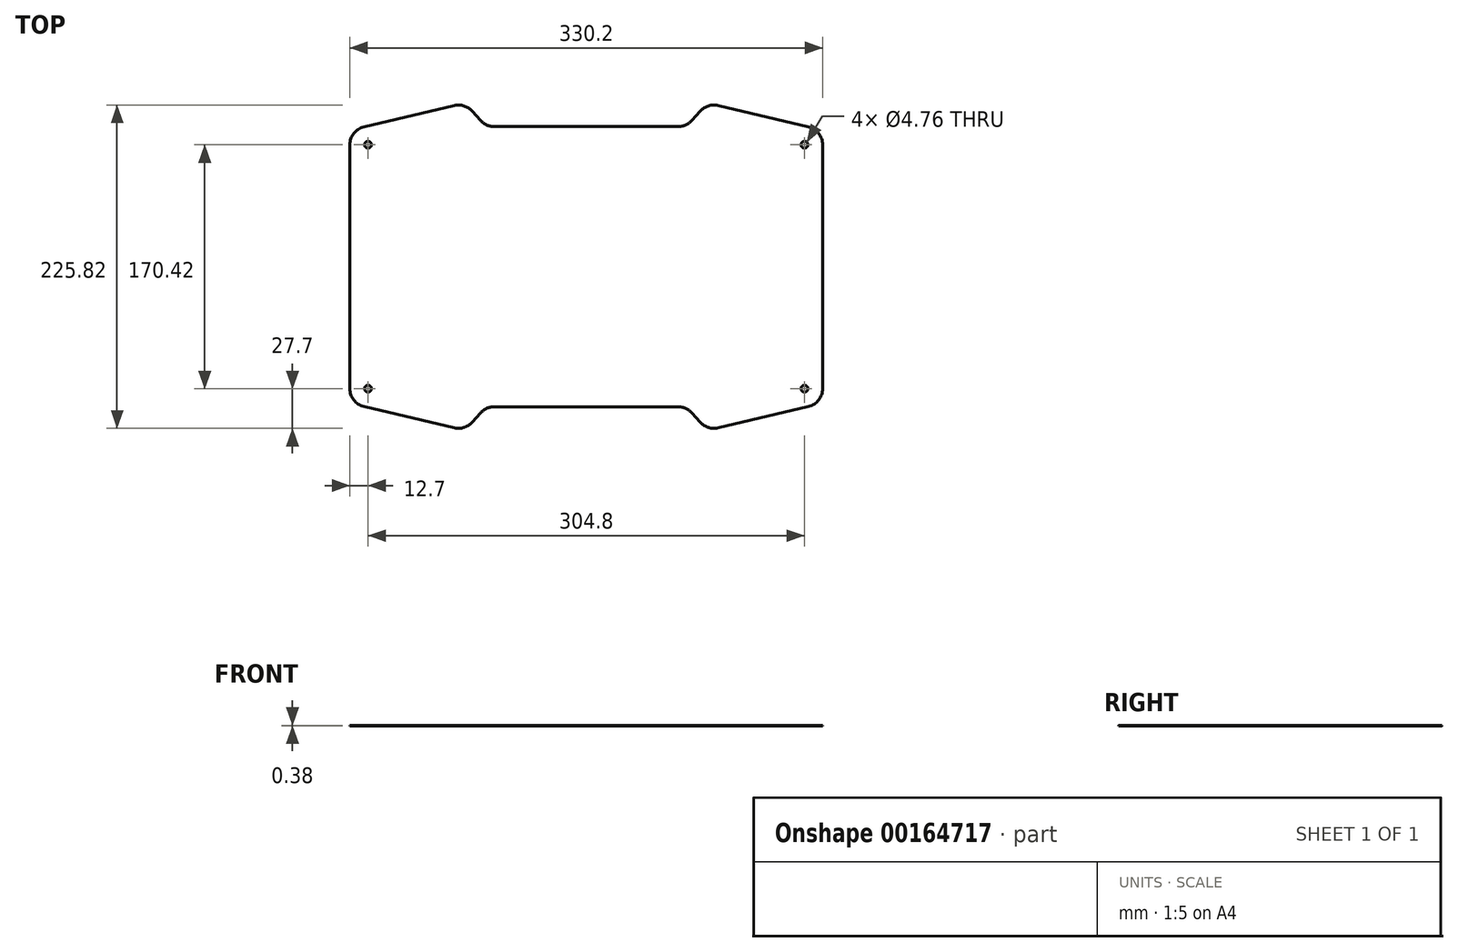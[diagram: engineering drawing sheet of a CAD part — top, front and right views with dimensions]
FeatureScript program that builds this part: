
annotation { "Feature Type Name" : "Feature", "Feature Type Description" : "" }
export const myFeature = defineFeature(function(context is Context, id is Id, definition is map)
    precondition{}
    {
        {
            var Q0;
            Q0=qCreatedBy(makeId("Top.planeOp"),FACE);
            var sketch = newSketch(context, id + "F0", { "sketchPlane" : qUnion([Q0])});
            skLineSegment(sketch, "E0.left", {"start": v(165.1, 95.25) * mm, "end": v(165.1, -95.25) * mm});
            skLineSegment(sketch, "E0.right", {"start": v(-165.1, 95.25) * mm, "end": v(-165.1, -95.25) * mm});
            skPoint(sketch, "E0.middle", {"position": v(0, 0) * mm});
            skLineSegment(sketch, "E1", {"start": v(-165.1, 95.25) * mm, "end": v(-84.78, 114.3) * mm});
            skLineSegment(sketch, "E2", {"start": v(-84.78, 114.3) * mm, "end": v(-69.85, 97.88) * mm});
            skLineSegment(sketch, "E3", {"start": v(-69.85, 97.88) * mm, "end": v(0, 97.88) * mm});
            skLineSegment(sketch, "E4.MirrorCS", {"start": v(165.1, 95.25) * mm, "end": v(84.78, 114.3) * mm});
            skLineSegment(sketch, "E5.MirrorCS", {"start": v(84.78, 114.3) * mm, "end": v(69.85, 97.88) * mm});
            skLineSegment(sketch, "E6.MirrorCS", {"start": v(69.85, 97.88) * mm, "end": v(0, 97.88) * mm});
            skLineSegment(sketch, "E7.MirrorCS", {"start": v(-165.1, -95.25) * mm, "end": v(-84.78, -114.3) * mm});
            skLineSegment(sketch, "E8.MirrorCS", {"start": v(-84.78, -114.3) * mm, "end": v(-69.85, -97.88) * mm});
            skLineSegment(sketch, "E9.MirrorCS", {"start": v(-69.85, -97.88) * mm, "end": v(0, -97.88) * mm});
            skLineSegment(sketch, "E10.MirrorCS", {"start": v(69.85, -97.88) * mm, "end": v(0, -97.88) * mm});
            skLineSegment(sketch, "E11.MirrorCS", {"start": v(84.78, -114.3) * mm, "end": v(69.85, -97.88) * mm});
            skLineSegment(sketch, "E12.MirrorCS", {"start": v(165.1, -95.25) * mm, "end": v(84.78, -114.3) * mm});
            skPoint(sketch, "E13.orphan", {"position": v(-165.1, 114.3) * mm});
            skPoint(sketch, "E14.orphan", {"position": v(165.1, 114.3) * mm});
            skPoint(sketch, "E15.orphan", {"position": v(165.1, -114.3) * mm});
            skPoint(sketch, "E16.orphan", {"position": v(-165.1, -114.3) * mm});
            skSolve(sketch);
        }
        {
            var Q0;
            Q0 = qSketchRegion(id + "F0", true);
            extrude(context, id + "F1", {"entities" : qUnion([Q0]), "depth" : 0.38 * mm});
        }
        {
            var Q0;
            Q0=makeQuery(id+"F1.opExtrude","SWEPT_EDGE",EDGE,{"disambiguationData":[OSD([sQuery(id+"F0.wireOp",EDGE,"E0.right"),sQuery(id+"F0.wireOp",EDGE,"E7.MirrorCS")])]});
            var Q1;
            Q1=makeQuery(id+"F1.opExtrude","SWEPT_EDGE",EDGE,{"disambiguationData":[OSD([sQuery(id+"F0.wireOp",EDGE,"E7.MirrorCS"),sQuery(id+"F0.wireOp",EDGE,"E8.MirrorCS")])]});
            var Q2;
            Q2=makeQuery(id+"F1.opExtrude","SWEPT_EDGE",EDGE,{"disambiguationData":[OSD([sQuery(id+"F0.wireOp",EDGE,"E8.MirrorCS"),sQuery(id+"F0.wireOp",EDGE,"E9.MirrorCS")])]});
            var Q3;
            Q3=makeQuery(id+"F1.opExtrude","SWEPT_EDGE",EDGE,{"disambiguationData":[OSD([sQuery(id+"F0.wireOp",EDGE,"E10.MirrorCS"),sQuery(id+"F0.wireOp",EDGE,"E11.MirrorCS")])]});
            var Q4;
            Q4=makeQuery(id+"F1.opExtrude","SWEPT_EDGE",EDGE,{"disambiguationData":[OSD([sQuery(id+"F0.wireOp",EDGE,"E11.MirrorCS"),sQuery(id+"F0.wireOp",EDGE,"E12.MirrorCS")])]});
            var Q5;
            Q5=makeQuery(id+"F1.opExtrude","SWEPT_EDGE",EDGE,{"disambiguationData":[OSD([sQuery(id+"F0.wireOp",EDGE,"E0.left"),sQuery(id+"F0.wireOp",EDGE,"E12.MirrorCS")])]});
            var Q6;
            Q6=makeQuery(id+"F1.opExtrude","SWEPT_EDGE",EDGE,{"disambiguationData":[OSD([sQuery(id+"F0.wireOp",EDGE,"E0.left"),sQuery(id+"F0.wireOp",EDGE,"E4.MirrorCS")])]});
            var Q7;
            Q7=makeQuery(id+"F1.opExtrude","SWEPT_EDGE",EDGE,{"disambiguationData":[OSD([sQuery(id+"F0.wireOp",EDGE,"E4.MirrorCS"),sQuery(id+"F0.wireOp",EDGE,"E5.MirrorCS")])]});
            var Q8;
            Q8=makeQuery(id+"F1.opExtrude","SWEPT_EDGE",EDGE,{"disambiguationData":[OSD([sQuery(id+"F0.wireOp",EDGE,"E5.MirrorCS"),sQuery(id+"F0.wireOp",EDGE,"E6.MirrorCS")])]});
            var Q9;
            Q9=makeQuery(id+"F1.opExtrude","SWEPT_EDGE",EDGE,{"disambiguationData":[OSD([sQuery(id+"F0.wireOp",EDGE,"E2"),sQuery(id+"F0.wireOp",EDGE,"E3")])]});
            var Q10;
            Q10=makeQuery(id+"F1.opExtrude","SWEPT_EDGE",EDGE,{"disambiguationData":[OSD([sQuery(id+"F0.wireOp",EDGE,"E1"),sQuery(id+"F0.wireOp",EDGE,"E2")])]});
            var Q11;
            Q11=makeQuery(id+"F1.opExtrude","SWEPT_EDGE",EDGE,{"disambiguationData":[OSD([sQuery(id+"F0.wireOp",EDGE,"E0.right"),sQuery(id+"F0.wireOp",EDGE,"E1")])]});
            fillet(context, id + "F2", {"entities" : qUnion([Q0, Q1, Q2, Q3, Q4, Q5, Q6, Q7, Q8, Q9, Q10, Q11]), "radius" : 12.7 * mm, "tangentPropagation" : true, "allowEdgeOverflow" : false});
        }
        {
            var Q0;
            Q0=makeQuery(id+"F1.opExtrude","CAP_FACE",FACE,{"disambiguationData":[OSD([sQuery(id+"F0.wireOp",EDGE,"E0.left"),sQuery(id+"F0.wireOp",EDGE,"E0.right"),sQuery(id+"F0.wireOp",EDGE,"E1"),sQuery(id+"F0.wireOp",EDGE,"E2"),sQuery(id+"F0.wireOp",EDGE,"E3"),sQuery(id+"F0.wireOp",EDGE,"E4.MirrorCS"),sQuery(id+"F0.wireOp",EDGE,"E5.MirrorCS"),sQuery(id+"F0.wireOp",EDGE,"E6.MirrorCS"),sQuery(id+"F0.wireOp",EDGE,"E7.MirrorCS"),sQuery(id+"F0.wireOp",EDGE,"E8.MirrorCS"),sQuery(id+"F0.wireOp",EDGE,"E9.MirrorCS"),sQuery(id+"F0.wireOp",EDGE,"E10.MirrorCS"),sQuery(id+"F0.wireOp",EDGE,"E11.MirrorCS"),sQuery(id+"F0.wireOp",EDGE,"E12.MirrorCS")])],"isStart":false});
            var sketch = newSketch(context, id + "F3", { "sketchPlane" : qUnion([Q0])});
            skPoint(sketch, "E17", {"position": v(152.4, -85.2) * mm});
            skPoint(sketch, "E18.MirrorP", {"position": v(-152.4, -85.2) * mm});
            skPoint(sketch, "E19.MirrorP", {"position": v(152.4, 85.2) * mm});
            skPoint(sketch, "E20.MirrorP", {"position": v(-152.4, 85.2) * mm});
            skSolve(sketch);
        }
        {
            var Q0;
            Q0=sQuery(id+"F3.wireOp",VERTEX,"E17");
            var Q1;
            Q1=sQuery(id+"F3.wireOp",VERTEX,"E18.MirrorP");
            var Q2;
            Q2=sQuery(id+"F3.wireOp",VERTEX,"E20.MirrorP");
            var Q3;
            Q3=sQuery(id+"F3.wireOp",VERTEX,"E19.MirrorP");
            var Q4;
            Q4=makeQuery(id+"F1.opExtrude","SWEPT_BODY",BODY,{"disambiguationData":[OSD([sQuery(id+"F0.wireOp",EDGE,"E0.left"),sQuery(id+"F0.wireOp",EDGE,"E0.right"),sQuery(id+"F0.wireOp",EDGE,"E1"),sQuery(id+"F0.wireOp",EDGE,"E2"),sQuery(id+"F0.wireOp",EDGE,"E3"),sQuery(id+"F0.wireOp",EDGE,"E4.MirrorCS"),sQuery(id+"F0.wireOp",EDGE,"E5.MirrorCS"),sQuery(id+"F0.wireOp",EDGE,"E6.MirrorCS"),sQuery(id+"F0.wireOp",EDGE,"E7.MirrorCS"),sQuery(id+"F0.wireOp",EDGE,"E8.MirrorCS"),sQuery(id+"F0.wireOp",EDGE,"E9.MirrorCS"),sQuery(id+"F0.wireOp",EDGE,"E10.MirrorCS"),sQuery(id+"F0.wireOp",EDGE,"E11.MirrorCS"),sQuery(id+"F0.wireOp",EDGE,"E12.MirrorCS")])]});
            hole(context, id + "F4", {"style" : HoleStyle.SIMPLE, "endStyle" : HoleEndStyle.BLIND, "holeDiameter" : 4.76 * mm, "holeDepth" : 6.73 * mm, "locations" : qUnion([Q0, Q1, Q2, Q3]), "scope" : qUnion([Q4])});
        }
    });
